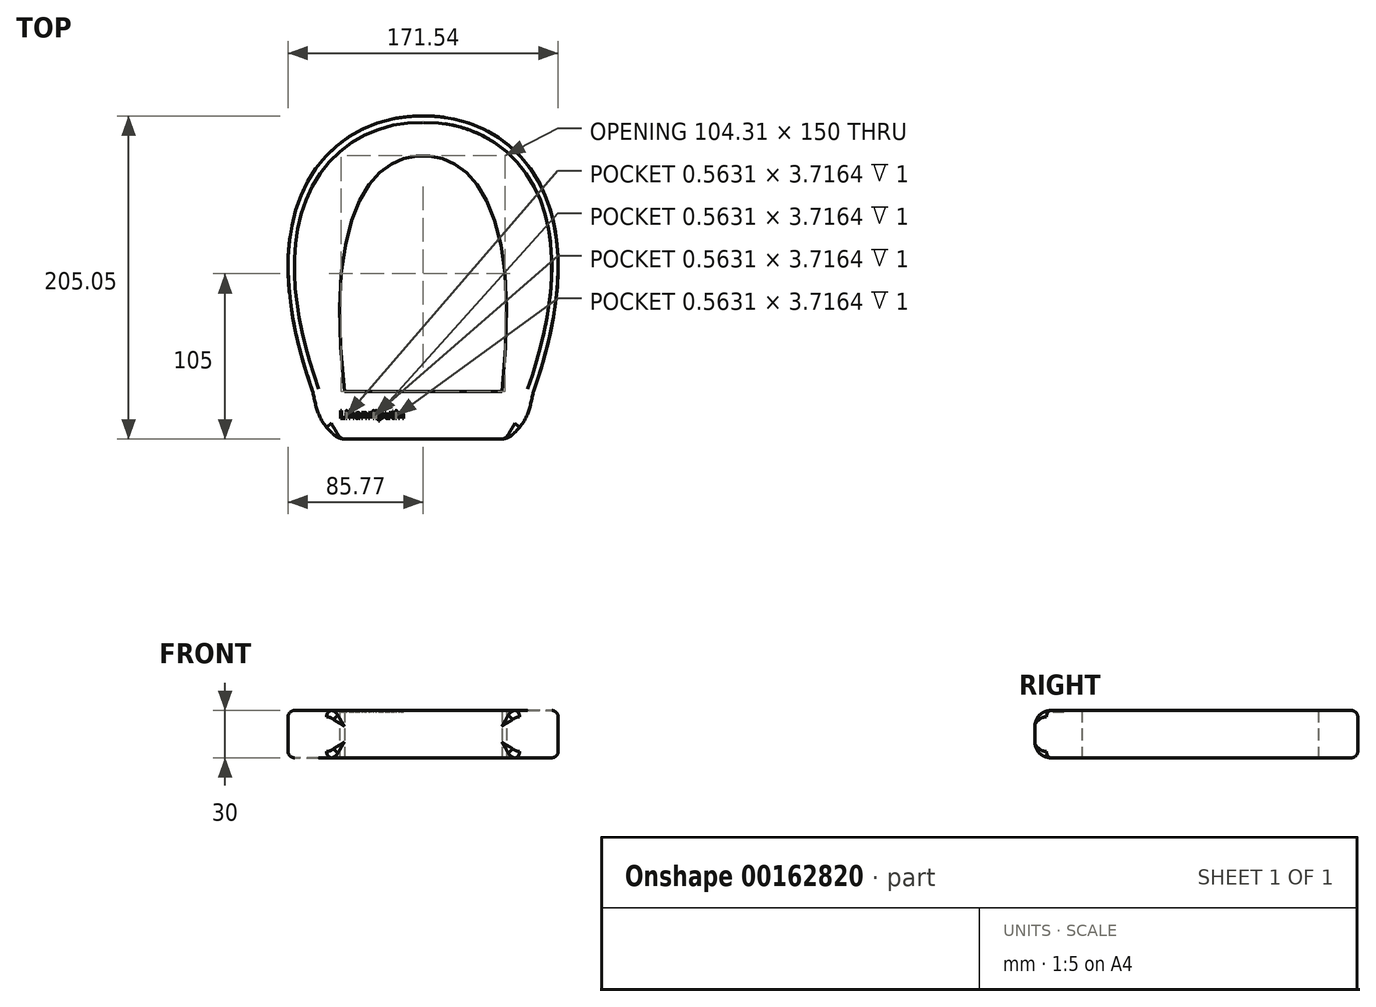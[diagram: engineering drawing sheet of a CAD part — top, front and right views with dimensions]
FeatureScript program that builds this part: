
annotation { "Feature Type Name" : "Feature", "Feature Type Description" : "" }
export const myFeature = defineFeature(function(context is Context, id is Id, definition is map)
    precondition{}
    {
        {
            var Q0;
            Q0=qCreatedBy(makeId("Top.planeOp"),FACE);
            var sketch = newSketch(context, id + "F0", { "sketchPlane" : qUnion([Q0])});
            skLineSegment(sketch, "E0", {"start": v(-100, 0) * mm, "end": v(0, 0) * mm});
            skLineSegment(sketch, "E1", {"start": v(-50, 0) * mm, "end": v(-50, -30) * mm, "construction": true});
            skLineSegment(sketch, "E2", {"start": v(-50, -30) * mm, "end": v(-103.77, -30) * mm});
            skLineSegment(sketch, "E3.MirrorCS", {"start": v(-50, -30) * mm, "end": v(3.77, -30) * mm});
            skLineSegment(sketch, "E4", {"start": v(-50, 0) * mm, "end": v(-50, 150) * mm, "construction": true});
            skLineSegment(sketch, "E5", {"start": v(-120, 0) * mm, "end": v(-100, 0) * mm, "construction": true});
            skLineSegment(sketch, "E6.MirrorCS", {"start": v(20, 0) * mm, "end": v(0, 0) * mm, "construction": true});
            skLineSegment(sketch, "E7", {"start": v(-50, 150) * mm, "end": v(-50, 175) * mm, "construction": true});
            skFitSpline(sketch, "E8", {"points": [v(-120, 0) * mm, v(20, 0) * mm], "startDerivative": vector(140, 0) * mm, "endDerivative": vector(140, 0) * mm});
            skFitSpline(sketch, "E9", {"points": [v(-120, 0) * mm, v(-50, 175) * mm, v(20, 0) * mm], "startDerivative": vector(-38.14, 753.42) * mm, "endDerivative": vector(-282.46, -794.07) * mm});
            skFitSpline(sketch, "E10.MirrorCS", {"points": [v(20, 0) * mm, v(-50, 175) * mm, v(-120, 0) * mm], "startDerivative": vector(38.14, 753.42) * mm, "endDerivative": vector(282.46, -794.07) * mm});
            skFitSpline(sketch, "E11.MirrorCS", {"points": [v(20, 0) * mm, v(-50, 175) * mm, v(-120, 0) * mm], "startDerivative": vector(38.14, 753.42) * mm, "endDerivative": vector(282.46, -794.07) * mm});
            skFitSpline(sketch, "E12", {"points": [v(-100, 0) * mm, v(0, 0) * mm], "startDerivative": vector(100, 0) * mm, "endDerivative": vector(100, 0) * mm});
            skFitSpline(sketch, "E13", {"points": [v(-100, 0) * mm, v(-50, 150) * mm, v(0, 0) * mm], "startDerivative": vector(-78.66, 695.27) * mm, "endDerivative": vector(-78.66, -695.27) * mm});
            skFitSpline(sketch, "E14", {"points": [v(-120, 0) * mm, v(-114.55, -18) * mm, v(-103.77, -30) * mm], "startDerivative": vector(7.41, -37.17) * mm, "endDerivative": vector(25.27, -22.64) * mm});
            skFitSpline(sketch, "E15.MirrorCS", {"points": [v(20, 0) * mm, v(14.55, -18) * mm, v(3.77, -30) * mm], "startDerivative": vector(-7.41, -37.17) * mm, "endDerivative": vector(-25.27, -22.64) * mm});
            skPoint(sketch, "E16.end.orphan", {"position": v(-120, -30) * mm});
            skPoint(sketch, "E17.MirrorCS.start.orphan", {"position": v(20, -30) * mm});
            skSolve(sketch);
        }
        {
            var Q0;
            Q0 = qSketchRegion(id + "F0", true);
            extrude(context, id + "F1", {"entities" : qUnion([Q0]), "depth" : 30 * mm});
        }
        {
            var Q0;
            Q0=makeQuery(id+"F1.opExtrude","SWEPT_FACE",FACE,{"disambiguationData":[OSD([sQuery(id+"F0.wireOp",EDGE,"E12")])]});
            var Q1;
            Q1=makeQuery(id+"F1.opExtrude","SWEPT_FACE",FACE,{"disambiguationData":[OSD([sQuery(id+"F0.wireOp",EDGE,"E2"),sQuery(id+"F0.wireOp",EDGE,"E3.MirrorCS")])]});
            fillet(context, id + "F2", {"entities" : qUnion([Q0, Q1]), "radius" : 10 * mm, "tangentPropagation" : true, "allowEdgeOverflow" : false});
        }
        {
            var Q0;
            Q0=makeQuery(id+"F1.opExtrude","SWEPT_FACE",FACE,{"disambiguationData":[OSD([sQuery(id+"F0.wireOp",EDGE,"E15.MirrorCS")])]});
            var Q1;
            Q1=makeQuery(id+"F1.opExtrude","SWEPT_FACE",FACE,{"disambiguationData":[OSD([sQuery(id+"F0.wireOp",EDGE,"E10.MirrorCS")])]});
            var Q2;
            Q2=makeQuery(id+"F1.opExtrude","SWEPT_FACE",FACE,{"disambiguationData":[OSD([sQuery(id+"F0.wireOp",EDGE,"E14")])]});
            var Q3;
            Q3=makeQuery(id+"F1.opExtrude","SWEPT_FACE",FACE,{"disambiguationData":[OSD([sQuery(id+"F0.wireOp",EDGE,"E9")])]});
            fillet(context, id + "F3", {"entities" : qUnion([Q0, Q1, Q2, Q3]), "radius" : 4 * mm, "tangentPropagation" : true, "allowEdgeOverflow" : false});
        }
        {
            var Q0;
            Q0=makeQuery(id+"F1.opExtrude","CAP_FACE",FACE,{"disambiguationData":[OSD([sQuery(id+"F0.wireOp",EDGE,"E2"),sQuery(id+"F0.wireOp",EDGE,"E3.MirrorCS"),sQuery(id+"F0.wireOp",EDGE,"E9"),sQuery(id+"F0.wireOp",EDGE,"E10.MirrorCS"),sQuery(id+"F0.wireOp",EDGE,"E12"),sQuery(id+"F0.wireOp",EDGE,"E13"),sQuery(id+"F0.wireOp",EDGE,"E14"),sQuery(id+"F0.wireOp",EDGE,"E15.MirrorCS")])],"isStart":false});
            var sketch = newSketch(context, id + "F4", { "sketchPlane" : qUnion([Q0])});
            skText(sketch, "E18", { "text": "Lihanriiputin", "fontName": "OpenSans-Regular.ttf"});
            const initialGuessF4  = {"E18": [-0.10302, -0.01693, 1, 0, 0.005]};
            skSetInitialGuess(sketch, initialGuessF4);
            skSolve(sketch);
        }
        {
            var Q0;
            Q0 = qSketchRegion(id + "F4", true);
            extrude(context, id + "F5", {"entities" : qUnion([Q0]), "operationType" : NewBodyOperationType.REMOVE, "oppositeDirection" : true, "depth" : 1 * mm});
        }
    });
